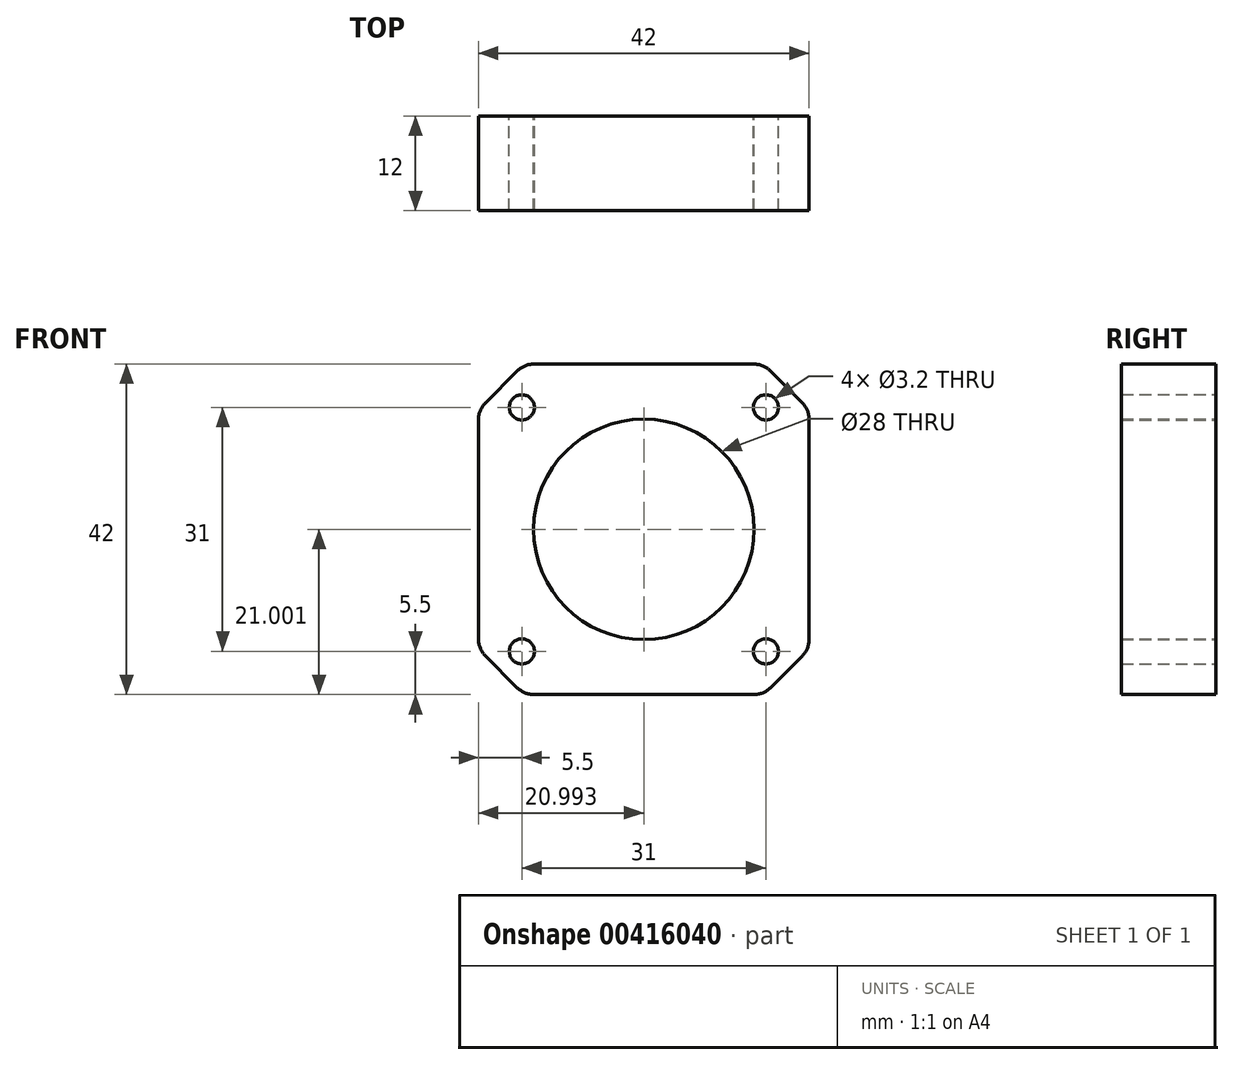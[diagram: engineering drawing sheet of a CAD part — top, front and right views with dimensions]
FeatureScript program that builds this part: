
annotation { "Feature Type Name" : "Feature", "Feature Type Description" : "" }
export const myFeature = defineFeature(function(context is Context, id is Id, definition is map)
    precondition{}
    {
        {
            var Q0;
            Q0=qCreatedBy(makeId("Front.planeOp"),FACE);
            var sketch = newSketch(context, id + "F0", { "sketchPlane" : qUnion([Q0])});
            skLineSegment(sketch, "E0.bottom", {"start": v(21, -21) * mm, "end": v(-21, -21) * mm});
            skLineSegment(sketch, "E0.top", {"start": v(21, 21) * mm, "end": v(-21, 21) * mm});
            skLineSegment(sketch, "E0.left", {"start": v(21, -21) * mm, "end": v(21, 21) * mm});
            skLineSegment(sketch, "E0.right", {"start": v(-21, -21) * mm, "end": v(-21, 21) * mm});
            skPoint(sketch, "E0.middle", {"position": v(0, 0) * mm});
            skCircle(sketch, "E1", {"center": v(-15.5, -15.5) * mm, "radius": 1.6 * mm});
            skPoint(sketch, "E1.first.point", {"position": v(-16.8, -14.57) * mm});
            skPoint(sketch, "E1.second.point", {"position": v(-13.92, -15.27) * mm});
            skPoint(sketch, "E1.third.point", {"position": v(-15.32, -17.09) * mm});
            skCircle(sketch, "E2", {"center": v(15.5, -15.5) * mm, "radius": 1.6 * mm});
            skPoint(sketch, "E2.first.point", {"position": v(14.22, -14.55) * mm});
            skPoint(sketch, "E2.second.point", {"position": v(17.06, -15.13) * mm});
            skPoint(sketch, "E2.third.point", {"position": v(15.08, -17.05) * mm});
            skCircle(sketch, "E3", {"center": v(15.5, 15.5) * mm, "radius": 1.6 * mm});
            skPoint(sketch, "E3.first.point", {"position": v(14.45, 16.7) * mm});
            skPoint(sketch, "E3.second.point", {"position": v(16.88, 16.3) * mm});
            skPoint(sketch, "E3.third.point", {"position": v(15.65, 13.9) * mm});
            skCircle(sketch, "E4", {"center": v(-15.5, 15.5) * mm, "radius": 1.6 * mm});
            skPoint(sketch, "E4.first.point", {"position": v(-16.8, 16.43) * mm});
            skPoint(sketch, "E4.second.point", {"position": v(-14.02, 16.1) * mm});
            skPoint(sketch, "E4.third.point", {"position": v(-15.65, 13.9) * mm});
            skCircle(sketch, "E5", {"center": v(0, 0) * mm, "radius": 14 * mm});
            skPoint(sketch, "E5.first.point", {"position": v(-10.66, 9.09) * mm});
            skPoint(sketch, "E5.second.point", {"position": v(12.57, 6.16) * mm});
            skPoint(sketch, "E5.third.point", {"position": v(-0.27, -14) * mm});
            skLineSegment(sketch, "E6", {"start": v(-21, -15.2) * mm, "end": v(21, -15.2) * mm, "construction": true});
            skLineSegment(sketch, "E7", {"start": v(-21, 15.2) * mm, "end": v(21, 15.2) * mm, "construction": true});
            skLineSegment(sketch, "E8", {"start": v(-15.2, 21) * mm, "end": v(-15.2, -21) * mm, "construction": true});
            skLineSegment(sketch, "E9", {"start": v(15.2, 21) * mm, "end": v(15.2, -21) * mm, "construction": true});
            skLineSegment(sketch, "E10", {"start": v(-21, 15.2) * mm, "end": v(-15.2, 21) * mm});
            skLineSegment(sketch, "E11", {"start": v(15.2, 21) * mm, "end": v(21, 15.2) * mm});
            skLineSegment(sketch, "E12", {"start": v(21, -15.2) * mm, "end": v(15.2, -21) * mm});
            skLineSegment(sketch, "E13", {"start": v(-15.2, -21) * mm, "end": v(-21, -15.2) * mm});
            skSolve(sketch);
        }
        {
            var Q0;
            Q0=makeQuery(id+"F0.imprint","IMPRINT",FACE,{"disambiguationData":[TD([[makeQuery(id+"F0.imprint","IMPRINT",EDGE,{"derivedFrom":sQuery(id+"F0.wireOp",EDGE,"E1")}),-1.0]])]});
            extrude(context, id + "F1", {"entities" : qUnion([Q0]), "depth" : 12 * mm});
        }
        {
            var Q0;
            Q0=makeQuery(id+"F1.opExtrude","SWEPT_EDGE",EDGE,{"disambiguationData":[OSD([sQuery(id+"F0.wireOp",EDGE,"E0.right"),sQuery(id+"F0.wireOp",EDGE,"E13")])]});
            var Q1;
            Q1=makeQuery(id+"F1.opExtrude","SWEPT_EDGE",EDGE,{"disambiguationData":[OSD([sQuery(id+"F0.wireOp",EDGE,"E0.bottom"),sQuery(id+"F0.wireOp",EDGE,"E13")])]});
            var Q2;
            Q2=makeQuery(id+"F1.opExtrude","SWEPT_EDGE",EDGE,{"disambiguationData":[OSD([sQuery(id+"F0.wireOp",EDGE,"E0.bottom"),sQuery(id+"F0.wireOp",EDGE,"E12")])]});
            var Q3;
            Q3=makeQuery(id+"F1.opExtrude","SWEPT_EDGE",EDGE,{"disambiguationData":[OSD([sQuery(id+"F0.wireOp",EDGE,"E0.left"),sQuery(id+"F0.wireOp",EDGE,"E12")])]});
            var Q4;
            Q4=makeQuery(id+"F1.opExtrude","SWEPT_EDGE",EDGE,{"disambiguationData":[OSD([sQuery(id+"F0.wireOp",EDGE,"E0.left"),sQuery(id+"F0.wireOp",EDGE,"E11")])]});
            var Q5;
            Q5=makeQuery(id+"F1.opExtrude","SWEPT_EDGE",EDGE,{"disambiguationData":[OSD([sQuery(id+"F0.wireOp",EDGE,"E0.top"),sQuery(id+"F0.wireOp",EDGE,"E11")])]});
            var Q6;
            Q6=makeQuery(id+"F1.opExtrude","SWEPT_EDGE",EDGE,{"disambiguationData":[OSD([sQuery(id+"F0.wireOp",EDGE,"E0.right"),sQuery(id+"F0.wireOp",EDGE,"E10")])]});
            var Q7;
            Q7=makeQuery(id+"F1.opExtrude","SWEPT_EDGE",EDGE,{"disambiguationData":[OSD([sQuery(id+"F0.wireOp",EDGE,"E0.top"),sQuery(id+"F0.wireOp",EDGE,"E10")])]});
            fillet(context, id + "F2", {"entities" : qUnion([Q0, Q1, Q2, Q3, Q4, Q5, Q6, Q7]), "radius" : 3 * mm, "tangentPropagation" : true, "allowEdgeOverflow" : false});
        }
    });
